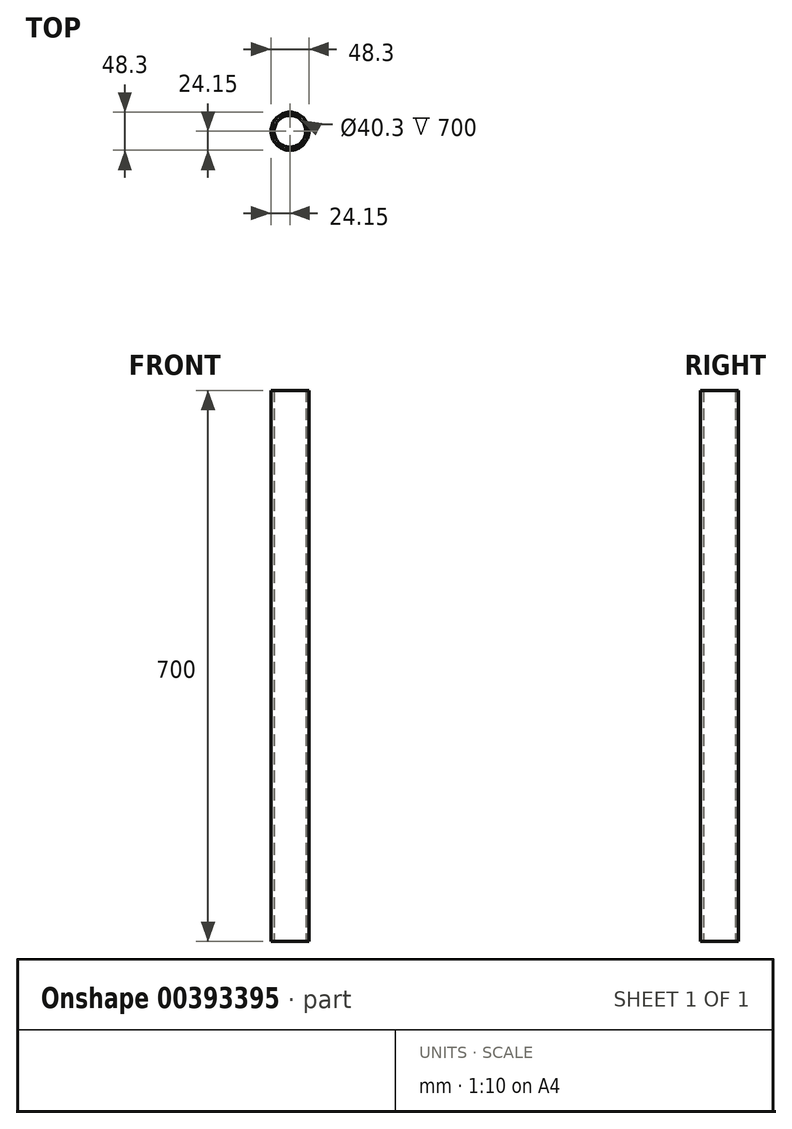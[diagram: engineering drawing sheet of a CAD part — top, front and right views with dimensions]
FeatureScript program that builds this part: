
annotation { "Feature Type Name" : "Feature", "Feature Type Description" : "" }
export const myFeature = defineFeature(function(context is Context, id is Id, definition is map)
    precondition{}
    {
        {
            var Q0;
            Q0=qCreatedBy(makeId("Top.planeOp"),FACE);
            var sketch = newSketch(context, id + "F0", { "sketchPlane" : qUnion([Q0])});
            skCircle(sketch, "E0", {"center": v(0, 0) * mm, "radius": 24.15 * mm});
            skCircle(sketch, "E1.0", {"center": v(0, 0) * mm, "radius": 20.15 * mm});
            skSolve(sketch);
        }
        {
            var Q0;
            Q0 = qSketchRegion(id + "F0", true);
            extrude(context, id + "F1", {"entities" : qUnion([Q0]), "depth" : 700 * mm});
        }
    });
